# Revit family: 1Doors_Mincey-Marble-Manufacturing_Napoli-6-Bowfront
name_source: partatom
category: Doors
units: mm (PartAtom-declared; Revit-internal decimal feet)

## family parameters
Always vertical = Yes
Cut with Voids When Loaded = No
OmniClass Number = 23.45.05.14.11.24
Room Calculation Point = No
Shared = No
Work Plane-Based = Yes

## types (1)
- NAPBF6 - 60 X 76 - Polished/Brushed/Black Matte - Clear/Frosted
    Angle = 45.24°
    Default Elevation = 48"
    Description = Frameless Bow Front Barn Door
    Fixed Panel Width = 30"
    Glass Material = Mincey Marble Manufacturing - Glass - Clear
    Glass Material Note = Available glass type: Clear, Frosted
    Height = 76"
    Height Note = Available custom sizes. Please, contact the manufacturer.
    Manufacturer = Mincey Marble Manufacturing
    Model = NAPBF6 - 60 X 76 - Polished/Brushed/Black Matte - Clear/Frosted
    Product Documentation Link = https://minceymarble.com
    Product Material = Mincey Marble Manufacturing - Metal - Polished
    Product Material Note = Available finishes: Polished, Brushed, Black Matte
    Product Page URL = https://minceymarble.com
    Radius = 78"
    Radius 1 = 77 13/16"
    Radius 2 = 78 3/16"
    Rough Height = 76"
    Rough Width = 60"
    Sliding Panel Width = 32 1/2"
    Thickness = 3"
    URL = https://minceymarble.com
    Version = 1
    Width = 60"
    Width Note = Available custom sizes. Please, contact the manufacturer.

## geometry (parser evidence)
native form markers: Sweep x7
no freeform markers — native parametric forms only
